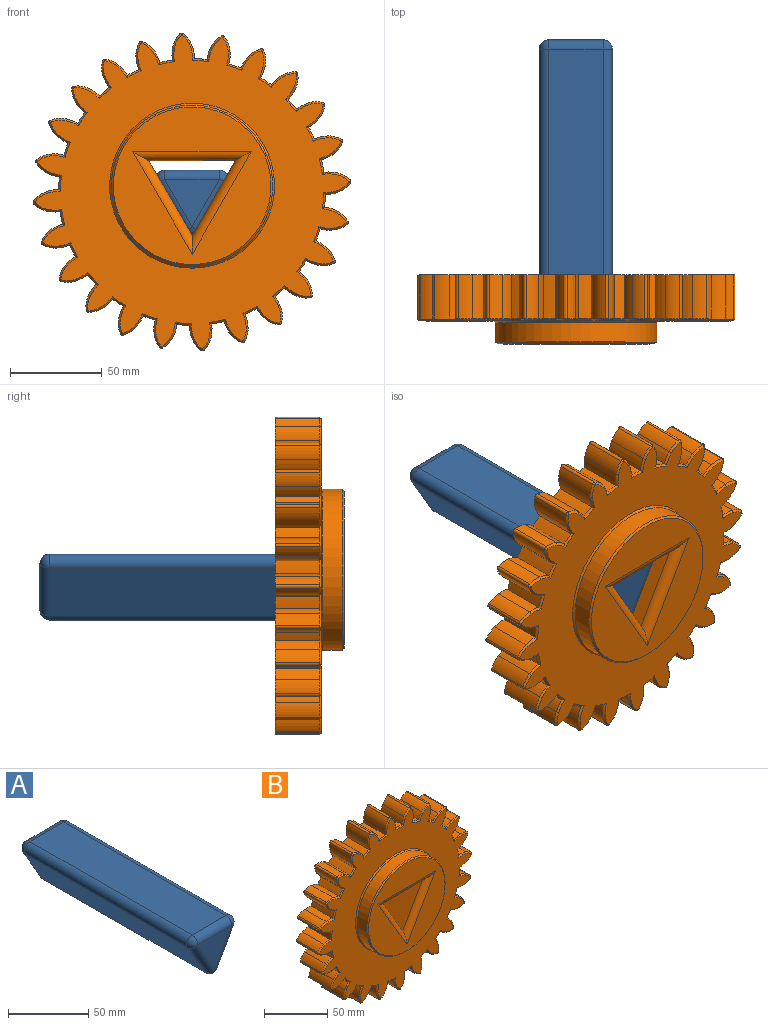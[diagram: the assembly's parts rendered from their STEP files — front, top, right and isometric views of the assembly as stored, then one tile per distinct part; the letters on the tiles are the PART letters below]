
ASSEMBLY  parts=2 mates=1
PART A: 20 faces, bbox 39.9x152.8x35.9 mm
  f0: plane 142.8x29.85mm, normal (0,0,1), area 4262.8mm2, adj f8,f13,f16,f19
  f1: plane 142.8x25.79mm, normal (-0.86,0,-0.5), area 4262.8mm2, adj f6,f14,f15,f19
  f2: plane 142.8x25.91mm, normal (0.87,0,-0.5), area 4262.8mm2, adj f5,f6,f7,f8
  f3: plane 29.85x25.91mm, normal (0,-1,0), area 385.9mm2, adj f5,f13,f14
  f4: plane 29.85x25.91mm, normal (0,1,0), area 385.9mm2, adj f7,f15,f16
  f5: cylinder r=5mm len=28.39mm, axis (-0.5,0,-0.87), area 234.5mm2, adj f2,f3,f9,f10
  f6: cylinder r=5mm len=142.8mm, axis (0,1,0), area 1495.4mm2, adj f1,f2,f10,f11
  f7: cylinder r=5mm len=28.39mm, axis (0.5,0,0.87), area 234.5mm2, adj f2,f4,f11,f12
  f8: cylinder r=5mm len=142.8mm, axis (0,1,0), area 1495.4mm2, adj f0,f2,f9,f12
  f9: sphere r=5mm, area 52.4mm2, adj f5,f8,f13
  f10: sphere r=5mm, area 52.4mm2, adj f5,f6,f14
  f11: sphere r=5mm, area 52.4mm2, adj f6,f7,f15
  f12: sphere r=5mm, area 52.4mm2, adj f7,f8,f16
  f13: cylinder r=5mm len=29.87mm, axis (1,0,0), area 234.5mm2, adj f0,f3,f9,f17
  f14: cylinder r=5mm len=28.31mm, axis (-0.5,0,0.86), area 234.5mm2, adj f1,f3,f10,f17
  f15: cylinder r=5mm len=28.31mm, axis (0.5,0,-0.86), area 234.5mm2, adj f1,f4,f11,f18
  f16: cylinder r=5mm len=29.87mm, axis (-1,0,0), area 234.5mm2, adj f0,f4,f12,f18
  f17: sphere r=5mm, area 52.3mm2, adj f13,f14,f19
  f18: sphere r=5mm, area 52.3mm2, adj f15,f16,f19
  f19: cylinder r=5mm len=142.8mm, axis (0,1,0), area 1495.4mm2, adj f0,f1,f17,f18
PART B: 300 faces, bbox 172.9x37.5x172.9 mm
  f0: cylinder r=72.52mm len=24mm, axis (0,1,0), area 165.9mm2, adj f29,f31,f95,f285
  f1: cylinder r=72.52mm len=24mm, axis (0,1,0), area 165.9mm2, adj f31,f90,f94,f297
  f2: cylinder r=72.52mm len=24mm, axis (0,1,0), area 165.9mm2, adj f31,f85,f89,f286
  f3: cylinder r=72.52mm len=24mm, axis (0,1,0), area 165.9mm2, adj f31,f80,f84,f274
  f4: cylinder r=72.52mm len=24mm, axis (0,1,0), area 165.9mm2, adj f31,f75,f79,f262
  f5: cylinder r=72.52mm len=24mm, axis (0,1,0), area 165.9mm2, adj f31,f70,f74,f250
  f6: cylinder r=72.52mm len=24mm, axis (0,1,0), area 165.9mm2, adj f31,f65,f69,f238
  f7: cylinder r=72.52mm len=24mm, axis (0,1,0), area 165.9mm2, adj f31,f60,f64,f226
  f8: cylinder r=72.52mm len=24mm, axis (0,1,0), area 165.9mm2, adj f31,f55,f59,f214
  f9: cylinder r=72.52mm len=24mm, axis (0,1,0), area 165.9mm2, adj f31,f50,f54,f202
  f10: cylinder r=72.52mm len=24mm, axis (0,1,0), area 165.9mm2, adj f31,f45,f49,f190
  f11: cylinder r=72.52mm len=24mm, axis (0,1,0), area 165.9mm2, adj f31,f40,f44,f178
  f12: cylinder r=72.52mm len=24mm, axis (0,1,0), area 165.9mm2, adj f31,f39,f146,f166
  f13: cylinder r=72.52mm len=24mm, axis (0,1,0), area 165.9mm2, adj f31,f145,f150,f154
  f14: cylinder r=72.52mm len=24mm, axis (0,1,0), area 165.9mm2, adj f31,f140,f144,f165
  f15: cylinder r=72.52mm len=24mm, axis (0,1,0), area 165.9mm2, adj f31,f135,f139,f177
  f16: cylinder r=72.52mm len=24mm, axis (0,1,0), area 165.9mm2, adj f31,f130,f134,f189
  f17: cylinder r=72.52mm len=24mm, axis (0,1,0), area 165.9mm2, adj f31,f125,f129,f201
  f18: cylinder r=72.52mm len=24mm, axis (0,1,0), area 165.9mm2, adj f31,f120,f124,f213
  f19: cylinder r=72.52mm len=24mm, axis (0,1,0), area 165.9mm2, adj f31,f115,f119,f225
  f20: cylinder r=72.52mm len=24mm, axis (0,1,0), area 165.9mm2, adj f31,f110,f114,f237
  f21: cylinder r=72.52mm len=24mm, axis (0,1,0), area 165.9mm2, adj f31,f105,f109,f249
  f22: cylinder r=72.52mm len=24mm, axis (0,1,0), area 165.9mm2, adj f31,f99,f104,f261
  f23: plane 40.76x32.5mm, normal (0.86,0,0.5), area 1533.1mm2, adj f31,f32,f35,f151
  f24: cylinder r=72.52mm len=24mm, axis (0,1,0), area 165.9mm2, adj f25,f31,f100,f273
  f25: cylinder r=18.6mm len=24mm, axis (0,1,0), area 174.8mm2, adj f24,f26,f31,f275
  f26: cylinder r=14.6mm len=24mm, axis (0,1,0), area 191.6mm2, adj f25,f27,f31,f277
  f27: cylinder r=1.39mm len=24mm, axis (0,1,0), area 56.5mm2, adj f26,f28,f31,f279
  f28: cylinder r=14.6mm len=24mm, axis (0,1,0), area 191.6mm2, adj f27,f29,f31,f281
  f29: cylinder r=21.66mm len=24mm, axis (0,1,0), area 174.3mm2, adj f0,f28,f31,f283
  f30: plane 170.88x170.88mm, normal (0,-1,0), area 12366.3mm2, adj f154,f155,f156,f157,f158,f159,f160,f161
  f31: plane 172.88x172.88mm, normal (0,1,0), area 18684mm2, adj f0,f1,f2,f3,f4,f5,f6,f7
  f32: plane 40.94x32.5mm, normal (-0.87,0,0.5), area 1533.1mm2, adj f23,f31,f35,f152
  f33: cylinder r=43.85mm len=87.7mm, axis (0,1,0), area 2892.9mm2, adj f298,f299
  f34: plane 85.7x85.7mm, normal (0,-1,0), area 3967.2mm2, adj f151,f152,f153,f299
  f35: plane 47.17x32.5mm, normal (0,0,-1), area 1533.1mm2, adj f23,f31,f32,f153
  f36: cylinder r=14.6mm len=24mm, axis (0,1,0), area 191.6mm2, adj f31,f37,f40,f174
  f37: cylinder r=1.39mm len=24mm, axis (0,1,0), area 56.5mm2, adj f31,f36,f38,f172
  f38: cylinder r=14.6mm len=24mm, axis (0,1,0), area 191.6mm2, adj f31,f37,f39,f170
  f39: cylinder r=21.66mm len=24mm, axis (0,1,0), area 174.3mm2, adj f12,f31,f38,f168
  f40: cylinder r=18.6mm len=24mm, axis (0,1,0), area 174.8mm2, adj f11,f31,f36,f176
  f41: cylinder r=14.6mm len=24mm, axis (0,1,0), area 191.6mm2, adj f31,f42,f45,f186
  f42: cylinder r=1.39mm len=24mm, axis (0,1,0), area 56.5mm2, adj f31,f41,f43,f184
  f43: cylinder r=14.6mm len=24mm, axis (0,1,0), area 191.6mm2, adj f31,f42,f44,f182
  f44: cylinder r=21.66mm len=24mm, axis (0,1,0), area 174.3mm2, adj f11,f31,f43,f180
  f45: cylinder r=18.6mm len=24mm, axis (0,1,0), area 174.8mm2, adj f10,f31,f41,f188
  f46: cylinder r=14.6mm len=24mm, axis (0,1,0), area 191.6mm2, adj f31,f47,f50,f198
  f47: cylinder r=1.39mm len=24mm, axis (0,1,0), area 56.5mm2, adj f31,f46,f48,f196
  f48: cylinder r=14.6mm len=24mm, axis (0,1,0), area 191.6mm2, adj f31,f47,f49,f194
  f49: cylinder r=21.66mm len=24mm, axis (0,1,0), area 174.3mm2, adj f10,f31,f48,f192
  f50: cylinder r=18.6mm len=24mm, axis (0,1,0), area 174.8mm2, adj f9,f31,f46,f200
  f51: cylinder r=14.6mm len=24mm, axis (0,1,0), area 191.6mm2, adj f31,f52,f55,f210
  f52: cylinder r=1.39mm len=24mm, axis (0,1,0), area 56.5mm2, adj f31,f51,f53,f208
  f53: cylinder r=14.6mm len=24mm, axis (0,1,0), area 191.6mm2, adj f31,f52,f54,f206
  f54: cylinder r=21.66mm len=24mm, axis (0,1,0), area 174.3mm2, adj f9,f31,f53,f204
  f55: cylinder r=18.6mm len=24mm, axis (0,1,0), area 174.8mm2, adj f8,f31,f51,f212
  f56: cylinder r=14.6mm len=24mm, axis (0,1,0), area 191.6mm2, adj f31,f57,f60,f222
  f57: cylinder r=1.39mm len=24mm, axis (0,1,0), area 56.5mm2, adj f31,f56,f58,f220
  f58: cylinder r=14.6mm len=24mm, axis (0,1,0), area 191.6mm2, adj f31,f57,f59,f218
  f59: cylinder r=21.66mm len=24mm, axis (0,1,0), area 174.3mm2, adj f8,f31,f58,f216
  f60: cylinder r=18.6mm len=24mm, axis (0,1,0), area 174.8mm2, adj f7,f31,f56,f224
  f61: cylinder r=14.6mm len=24mm, axis (0,1,0), area 191.6mm2, adj f31,f62,f65,f234
  f62: cylinder r=1.39mm len=24mm, axis (0,1,0), area 56.5mm2, adj f31,f61,f63,f232
  f63: cylinder r=14.6mm len=24mm, axis (0,1,0), area 191.6mm2, adj f31,f62,f64,f230
  f64: cylinder r=21.66mm len=24mm, axis (0,1,0), area 174.3mm2, adj f7,f31,f63,f228
  f65: cylinder r=18.6mm len=24mm, axis (0,1,0), area 174.8mm2, adj f6,f31,f61,f236
  f66: cylinder r=14.6mm len=24mm, axis (0,1,0), area 191.6mm2, adj f31,f67,f70,f246
  f67: cylinder r=1.39mm len=24mm, axis (0,1,0), area 56.5mm2, adj f31,f66,f68,f244
  f68: cylinder r=14.6mm len=24mm, axis (0,1,0), area 191.6mm2, adj f31,f67,f69,f242
  f69: cylinder r=21.66mm len=24mm, axis (0,1,0), area 174.3mm2, adj f6,f31,f68,f240
  f70: cylinder r=18.6mm len=24mm, axis (0,1,0), area 174.8mm2, adj f5,f31,f66,f248
  f71: cylinder r=14.6mm len=24mm, axis (0,1,0), area 191.6mm2, adj f31,f72,f75,f258
  f72: cylinder r=1.39mm len=24mm, axis (0,1,0), area 56.5mm2, adj f31,f71,f73,f256
  f73: cylinder r=14.6mm len=24mm, axis (0,1,0), area 191.6mm2, adj f31,f72,f74,f254
  f74: cylinder r=21.66mm len=24mm, axis (0,1,0), area 174.3mm2, adj f5,f31,f73,f252
  f75: cylinder r=18.6mm len=24mm, axis (0,1,0), area 174.8mm2, adj f4,f31,f71,f260
  f76: cylinder r=14.6mm len=24mm, axis (0,1,0), area 191.6mm2, adj f31,f77,f80,f270
  f77: cylinder r=1.39mm len=24mm, axis (0,1,0), area 56.5mm2, adj f31,f76,f78,f268
  f78: cylinder r=14.6mm len=24mm, axis (0,1,0), area 191.6mm2, adj f31,f77,f79,f266
  f79: cylinder r=21.66mm len=24mm, axis (0,1,0), area 174.3mm2, adj f4,f31,f78,f264
  f80: cylinder r=18.6mm len=24mm, axis (0,1,0), area 174.8mm2, adj f3,f31,f76,f272
  f81: cylinder r=14.6mm len=24mm, axis (0,1,0), area 191.6mm2, adj f31,f82,f85,f282
  f82: cylinder r=1.39mm len=24mm, axis (0,1,0), area 56.5mm2, adj f31,f81,f83,f280
  f83: cylinder r=14.6mm len=24mm, axis (0,1,0), area 191.6mm2, adj f31,f82,f84,f278
  f84: cylinder r=21.66mm len=24mm, axis (0,1,0), area 174.3mm2, adj f3,f31,f83,f276
  f85: cylinder r=18.6mm len=24mm, axis (0,1,0), area 174.8mm2, adj f2,f31,f81,f284
  f86: cylinder r=14.6mm len=24mm, axis (0,1,0), area 191.6mm2, adj f31,f87,f90,f294
  f87: cylinder r=1.39mm len=24mm, axis (0,1,0), area 56.5mm2, adj f31,f86,f88,f292
  f88: cylinder r=14.6mm len=24mm, axis (0,1,0), area 191.6mm2, adj f31,f87,f89,f290
  f89: cylinder r=21.66mm len=24mm, axis (0,1,0), area 174.3mm2, adj f2,f31,f88,f288
  f90: cylinder r=18.6mm len=24mm, axis (0,1,0), area 174.8mm2, adj f1,f31,f86,f296
  f91: cylinder r=14.6mm len=24mm, axis (0,1,0), area 191.6mm2, adj f31,f92,f95,f289
  f92: cylinder r=1.39mm len=24mm, axis (0,1,0), area 56.5mm2, adj f31,f91,f93,f291
  f93: cylinder r=14.6mm len=24mm, axis (0,1,0), area 191.6mm2, adj f31,f92,f94,f293
  f94: cylinder r=21.66mm len=24mm, axis (0,1,0), area 174.3mm2, adj f1,f31,f93,f295
  f95: cylinder r=18.6mm len=24mm, axis (0,1,0), area 174.8mm2, adj f0,f31,f91,f287
  f96: cylinder r=14.6mm len=24mm, axis (0,1,0), area 191.6mm2, adj f31,f97,f99,f265
  f97: cylinder r=1.39mm len=24mm, axis (0,1,0), area 56.5mm2, adj f31,f96,f98,f267
  f98: cylinder r=14.6mm len=24mm, axis (0,1,0), area 191.6mm2, adj f31,f97,f100,f269
  f99: cylinder r=18.6mm len=24mm, axis (0,1,0), area 174.8mm2, adj f22,f31,f96,f263
  f100: cylinder r=21.66mm len=24mm, axis (0,1,0), area 174.3mm2, adj f24,f31,f98,f271
  f101: cylinder r=14.6mm len=24mm, axis (0,1,0), area 191.6mm2, adj f31,f102,f105,f253
  f102: cylinder r=1.39mm len=24mm, axis (0,1,0), area 56.5mm2, adj f31,f101,f103,f255
  f103: cylinder r=14.6mm len=24mm, axis (0,1,0), area 191.6mm2, adj f31,f102,f104,f257
  f104: cylinder r=21.66mm len=24mm, axis (0,1,0), area 174.3mm2, adj f22,f31,f103,f259
  f105: cylinder r=18.6mm len=24mm, axis (0,1,0), area 174.8mm2, adj f21,f31,f101,f251
  f106: cylinder r=14.6mm len=24mm, axis (0,1,0), area 191.6mm2, adj f31,f107,f110,f241
  f107: cylinder r=1.39mm len=24mm, axis (0,1,0), area 56.5mm2, adj f31,f106,f108,f243
  f108: cylinder r=14.6mm len=24mm, axis (0,1,0), area 191.6mm2, adj f31,f107,f109,f245
  f109: cylinder r=21.66mm len=24mm, axis (0,1,0), area 174.3mm2, adj f21,f31,f108,f247
  f110: cylinder r=18.6mm len=24mm, axis (0,1,0), area 174.8mm2, adj f20,f31,f106,f239
  f111: cylinder r=14.6mm len=24mm, axis (0,1,0), area 191.6mm2, adj f31,f112,f115,f229
  f112: cylinder r=1.39mm len=24mm, axis (0,1,0), area 56.5mm2, adj f31,f111,f113,f231
  f113: cylinder r=14.6mm len=24mm, axis (0,1,0), area 191.6mm2, adj f31,f112,f114,f233
  f114: cylinder r=21.66mm len=24mm, axis (0,1,0), area 174.3mm2, adj f20,f31,f113,f235
  f115: cylinder r=18.6mm len=24mm, axis (0,1,0), area 174.8mm2, adj f19,f31,f111,f227
  f116: cylinder r=14.6mm len=24mm, axis (0,1,0), area 191.6mm2, adj f31,f117,f120,f217
  f117: cylinder r=1.39mm len=24mm, axis (0,1,0), area 56.5mm2, adj f31,f116,f118,f219
  f118: cylinder r=14.6mm len=24mm, axis (0,1,0), area 191.6mm2, adj f31,f117,f119,f221
  f119: cylinder r=21.66mm len=24mm, axis (0,1,0), area 174.3mm2, adj f19,f31,f118,f223
  f120: cylinder r=18.6mm len=24mm, axis (0,1,0), area 174.8mm2, adj f18,f31,f116,f215
  f121: cylinder r=14.6mm len=24mm, axis (0,1,0), area 191.6mm2, adj f31,f122,f125,f205
  f122: cylinder r=1.39mm len=24mm, axis (0,1,0), area 56.5mm2, adj f31,f121,f123,f207
  f123: cylinder r=14.6mm len=24mm, axis (0,1,0), area 191.6mm2, adj f31,f122,f124,f209
  f124: cylinder r=21.66mm len=24mm, axis (0,1,0), area 174.3mm2, adj f18,f31,f123,f211
  f125: cylinder r=18.6mm len=24mm, axis (0,1,0), area 174.8mm2, adj f17,f31,f121,f203
  f126: cylinder r=14.6mm len=24mm, axis (0,1,0), area 191.6mm2, adj f31,f127,f130,f193
  f127: cylinder r=1.39mm len=24mm, axis (0,1,0), area 56.5mm2, adj f31,f126,f128,f195
  f128: cylinder r=14.6mm len=24mm, axis (0,1,0), area 191.6mm2, adj f31,f127,f129,f197
  f129: cylinder r=21.66mm len=24mm, axis (0,1,0), area 174.3mm2, adj f17,f31,f128,f199
  f130: cylinder r=18.6mm len=24mm, axis (0,1,0), area 174.8mm2, adj f16,f31,f126,f191
  f131: cylinder r=14.6mm len=24mm, axis (0,1,0), area 191.6mm2, adj f31,f132,f135,f181
  f132: cylinder r=1.39mm len=24mm, axis (0,1,0), area 56.5mm2, adj f31,f131,f133,f183
  f133: cylinder r=14.6mm len=24mm, axis (0,1,0), area 191.6mm2, adj f31,f132,f134,f185
  f134: cylinder r=21.66mm len=24mm, axis (0,1,0), area 174.3mm2, adj f16,f31,f133,f187
  f135: cylinder r=18.6mm len=24mm, axis (0,1,0), area 174.8mm2, adj f15,f31,f131,f179
  f136: cylinder r=14.6mm len=24mm, axis (0,1,0), area 191.6mm2, adj f31,f137,f140,f169
  f137: cylinder r=1.39mm len=24mm, axis (0,1,0), area 56.5mm2, adj f31,f136,f138,f171
  f138: cylinder r=14.6mm len=24mm, axis (0,1,0), area 191.6mm2, adj f31,f137,f139,f173
  f139: cylinder r=21.66mm len=24mm, axis (0,1,0), area 174.3mm2, adj f15,f31,f138,f175
  f140: cylinder r=18.6mm len=24mm, axis (0,1,0), area 174.8mm2, adj f14,f31,f136,f167
  f141: cylinder r=14.6mm len=24mm, axis (0,1,0), area 191.6mm2, adj f31,f142,f145,f157
  f142: cylinder r=1.39mm len=24mm, axis (0,1,0), area 56.5mm2, adj f31,f141,f143,f159
  f143: cylinder r=14.6mm len=24mm, axis (0,1,0), area 191.6mm2, adj f31,f142,f144,f161
  f144: cylinder r=21.66mm len=24mm, axis (0,1,0), area 174.3mm2, adj f14,f31,f143,f163
  f145: cylinder r=18.6mm len=24mm, axis (0,1,0), area 174.8mm2, adj f13,f31,f141,f155
  f146: cylinder r=18.6mm len=24mm, axis (0,1,0), area 174.8mm2, adj f12,f31,f147,f164
  f147: cylinder r=14.6mm len=24mm, axis (0,1,0), area 191.6mm2, adj f31,f146,f148,f162
  f148: cylinder r=1.39mm len=24mm, axis (0,1,0), area 56.5mm2, adj f31,f147,f149,f160
  f149: cylinder r=14.6mm len=24mm, axis (0,1,0), area 191.6mm2, adj f31,f148,f150,f158
  f150: cylinder r=21.66mm len=24mm, axis (0,1,0), area 174.3mm2, adj f13,f31,f149,f156
  f151: cylinder r=5mm len=58.24mm, axis (0.5,0,-0.86), area 419.9mm2, adj f23,f34,f152,f153
  f152: cylinder r=5mm len=58.46mm, axis (0.5,0,0.87), area 419.9mm2, adj f32,f34,f151,f153
  f153: cylinder r=5mm len=64.51mm, axis (-1,0,0), area 419.9mm2, adj f34,f35,f151,f152
  f154: cone r=71.52mm half-angle=45deg, axis (0,1,0), area 11.1mm2, adj f13,f30,f155,f156
  f155: cone r=17.6mm half-angle=45deg, axis (0,1,0), area 10.8mm2, adj f30,f145,f154,f157
  f156: cone r=20.66mm half-angle=45deg, axis (0,1,0), area 10.7mm2, adj f30,f150,f154,f158
  f157: cone r=13.6mm half-angle=45deg, axis (0,1,0), area 11mm2, adj f30,f141,f155,f159
  f158: cone r=14.6mm half-angle=45deg, axis (0,1,0), area 11mm2, adj f30,f149,f156,f160
  f159: cone r=0.39mm half-angle=45deg, axis (0,1,0), area 2.2mm2, adj f30,f142,f157,f161
  f160: cone r=0.39mm half-angle=45deg, axis (0,1,0), area 2.2mm2, adj f30,f148,f158,f162
  f161: cone r=14.6mm half-angle=45deg, axis (0,1,0), area 11mm2, adj f30,f143,f159,f163
  f162: cone r=13.6mm half-angle=45deg, axis (0,1,0), area 11mm2, adj f30,f147,f160,f164
  f163: cone r=20.66mm half-angle=45deg, axis (0,1,0), area 10.7mm2, adj f30,f144,f161,f165
  f164: cone r=17.6mm half-angle=45deg, axis (0,1,0), area 10.8mm2, adj f30,f146,f162,f166
  f165: cone r=71.52mm half-angle=45deg, axis (0,1,0), area 11.1mm2, adj f14,f30,f163,f167
  f166: cone r=71.52mm half-angle=45deg, axis (0,1,0), area 11.1mm2, adj f12,f30,f164,f168
  f167: cone r=17.6mm half-angle=45deg, axis (0,1,0), area 10.8mm2, adj f30,f140,f165,f169
  f168: cone r=20.66mm half-angle=45deg, axis (0,1,0), area 10.7mm2, adj f30,f39,f166,f170
  f169: cone r=13.6mm half-angle=45deg, axis (0,1,0), area 11mm2, adj f30,f136,f167,f171
  f170: cone r=14.6mm half-angle=45deg, axis (0,1,0), area 11mm2, adj f30,f38,f168,f172
  f171: cone r=0.39mm half-angle=45deg, axis (0,1,0), area 2.2mm2, adj f30,f137,f169,f173
  f172: cone r=0.39mm half-angle=45deg, axis (0,1,0), area 2.2mm2, adj f30,f37,f170,f174
  f173: cone r=14.6mm half-angle=45deg, axis (0,1,0), area 11mm2, adj f30,f138,f171,f175
  f174: cone r=13.6mm half-angle=45deg, axis (0,1,0), area 11mm2, adj f30,f36,f172,f176
  f175: cone r=20.66mm half-angle=45deg, axis (0,1,0), area 10.7mm2, adj f30,f139,f173,f177
  f176: cone r=17.6mm half-angle=45deg, axis (0,1,0), area 10.8mm2, adj f30,f40,f174,f178
  f177: cone r=71.52mm half-angle=45deg, axis (0,1,0), area 11.1mm2, adj f15,f30,f175,f179
  f178: cone r=71.52mm half-angle=45deg, axis (0,1,0), area 11.1mm2, adj f11,f30,f176,f180
  f179: cone r=17.6mm half-angle=45deg, axis (0,1,0), area 10.8mm2, adj f30,f135,f177,f181
  f180: cone r=20.66mm half-angle=45deg, axis (0,1,0), area 10.7mm2, adj f30,f44,f178,f182
  f181: cone r=13.6mm half-angle=45deg, axis (0,1,0), area 11mm2, adj f30,f131,f179,f183
  f182: cone r=14.6mm half-angle=45deg, axis (0,1,0), area 11mm2, adj f30,f43,f180,f184
  f183: cone r=0.39mm half-angle=45deg, axis (0,1,0), area 2.2mm2, adj f30,f132,f181,f185
  f184: cone r=0.39mm half-angle=45deg, axis (0,1,0), area 2.2mm2, adj f30,f42,f182,f186
  f185: cone r=14.6mm half-angle=45deg, axis (0,1,0), area 11mm2, adj f30,f133,f183,f187
  f186: cone r=13.6mm half-angle=45deg, axis (0,1,0), area 11mm2, adj f30,f41,f184,f188
  f187: cone r=20.66mm half-angle=45deg, axis (0,1,0), area 10.7mm2, adj f30,f134,f185,f189
  f188: cone r=17.6mm half-angle=45deg, axis (0,1,0), area 10.8mm2, adj f30,f45,f186,f190
  f189: cone r=71.52mm half-angle=45deg, axis (0,1,0), area 11.1mm2, adj f16,f30,f187,f191
  f190: cone r=71.52mm half-angle=45deg, axis (0,1,0), area 11.1mm2, adj f10,f30,f188,f192
  f191: cone r=17.6mm half-angle=45deg, axis (0,1,0), area 10.8mm2, adj f30,f130,f189,f193
  f192: cone r=20.66mm half-angle=45deg, axis (0,1,0), area 10.7mm2, adj f30,f49,f190,f194
  f193: cone r=13.6mm half-angle=45deg, axis (0,1,0), area 11mm2, adj f30,f126,f191,f195
  f194: cone r=14.6mm half-angle=45deg, axis (0,1,0), area 11mm2, adj f30,f48,f192,f196
  f195: cone r=0.39mm half-angle=45deg, axis (0,1,0), area 2.2mm2, adj f30,f127,f193,f197
  f196: cone r=0.39mm half-angle=45deg, axis (0,1,0), area 2.2mm2, adj f30,f47,f194,f198
  f197: cone r=14.6mm half-angle=45deg, axis (0,1,0), area 11mm2, adj f30,f128,f195,f199
  f198: cone r=13.6mm half-angle=45deg, axis (0,1,0), area 11mm2, adj f30,f46,f196,f200
  f199: cone r=20.66mm half-angle=45deg, axis (0,1,0), area 10.7mm2, adj f30,f129,f197,f201
  f200: cone r=17.6mm half-angle=45deg, axis (0,1,0), area 10.8mm2, adj f30,f50,f198,f202
  f201: cone r=71.52mm half-angle=45deg, axis (0,1,0), area 11.1mm2, adj f17,f30,f199,f203
  f202: cone r=71.52mm half-angle=45deg, axis (0,1,0), area 11.1mm2, adj f9,f30,f200,f204
  f203: cone r=17.6mm half-angle=45deg, axis (0,1,0), area 10.8mm2, adj f30,f125,f201,f205
  f204: cone r=20.66mm half-angle=45deg, axis (0,1,0), area 10.7mm2, adj f30,f54,f202,f206
  f205: cone r=13.6mm half-angle=45deg, axis (0,1,0), area 11mm2, adj f30,f121,f203,f207
  f206: cone r=14.6mm half-angle=45deg, axis (0,1,0), area 11mm2, adj f30,f53,f204,f208
  f207: cone r=0.39mm half-angle=45deg, axis (0,1,0), area 2.2mm2, adj f30,f122,f205,f209
  f208: cone r=0.39mm half-angle=45deg, axis (0,1,0), area 2.2mm2, adj f30,f52,f206,f210
  f209: cone r=14.6mm half-angle=45deg, axis (0,1,0), area 11mm2, adj f30,f123,f207,f211
  f210: cone r=13.6mm half-angle=45deg, axis (0,1,0), area 11mm2, adj f30,f51,f208,f212
  f211: cone r=20.66mm half-angle=45deg, axis (0,1,0), area 10.7mm2, adj f30,f124,f209,f213
  f212: cone r=17.6mm half-angle=45deg, axis (0,1,0), area 10.8mm2, adj f30,f55,f210,f214
  f213: cone r=71.52mm half-angle=45deg, axis (0,1,0), area 11.1mm2, adj f18,f30,f211,f215
  f214: cone r=71.52mm half-angle=45deg, axis (0,1,0), area 11.1mm2, adj f8,f30,f212,f216
  f215: cone r=17.6mm half-angle=45deg, axis (0,1,0), area 10.8mm2, adj f30,f120,f213,f217
  f216: cone r=20.66mm half-angle=45deg, axis (0,1,0), area 10.7mm2, adj f30,f59,f214,f218
  f217: cone r=13.6mm half-angle=45deg, axis (0,1,0), area 11mm2, adj f30,f116,f215,f219
  f218: cone r=14.6mm half-angle=45deg, axis (0,1,0), area 11mm2, adj f30,f58,f216,f220
  f219: cone r=0.39mm half-angle=45deg, axis (0,1,0), area 2.2mm2, adj f30,f117,f217,f221
  f220: cone r=0.39mm half-angle=45deg, axis (0,1,0), area 2.2mm2, adj f30,f57,f218,f222
  f221: cone r=14.6mm half-angle=45deg, axis (0,1,0), area 11mm2, adj f30,f118,f219,f223
  f222: cone r=13.6mm half-angle=45deg, axis (0,1,0), area 11mm2, adj f30,f56,f220,f224
  f223: cone r=20.66mm half-angle=45deg, axis (0,1,0), area 10.7mm2, adj f30,f119,f221,f225
  f224: cone r=17.6mm half-angle=45deg, axis (0,1,0), area 10.8mm2, adj f30,f60,f222,f226
  f225: cone r=71.52mm half-angle=45deg, axis (0,1,0), area 11.1mm2, adj f19,f30,f223,f227
  f226: cone r=71.52mm half-angle=45deg, axis (0,1,0), area 11.1mm2, adj f7,f30,f224,f228
  f227: cone r=17.6mm half-angle=45deg, axis (0,1,0), area 10.8mm2, adj f30,f115,f225,f229
  f228: cone r=20.66mm half-angle=45deg, axis (0,1,0), area 10.7mm2, adj f30,f64,f226,f230
  f229: cone r=13.6mm half-angle=45deg, axis (0,1,0), area 11mm2, adj f30,f111,f227,f231
  f230: cone r=14.6mm half-angle=45deg, axis (0,1,0), area 11mm2, adj f30,f63,f228,f232
  f231: cone r=0.39mm half-angle=45deg, axis (0,1,0), area 2.2mm2, adj f30,f112,f229,f233
  f232: cone r=0.39mm half-angle=45deg, axis (0,1,0), area 2.2mm2, adj f30,f62,f230,f234
  f233: cone r=14.6mm half-angle=45deg, axis (0,1,0), area 11mm2, adj f30,f113,f231,f235
  f234: cone r=13.6mm half-angle=45deg, axis (0,1,0), area 11mm2, adj f30,f61,f232,f236
  f235: cone r=20.66mm half-angle=45deg, axis (0,1,0), area 10.7mm2, adj f30,f114,f233,f237
  f236: cone r=17.6mm half-angle=45deg, axis (0,1,0), area 10.8mm2, adj f30,f65,f234,f238
  f237: cone r=71.52mm half-angle=45deg, axis (0,1,0), area 11.1mm2, adj f20,f30,f235,f239
  f238: cone r=71.52mm half-angle=45deg, axis (0,1,0), area 11.1mm2, adj f6,f30,f236,f240
  f239: cone r=17.6mm half-angle=45deg, axis (0,1,0), area 10.8mm2, adj f30,f110,f237,f241
  f240: cone r=20.66mm half-angle=45deg, axis (0,1,0), area 10.7mm2, adj f30,f69,f238,f242
  f241: cone r=13.6mm half-angle=45deg, axis (0,1,0), area 11mm2, adj f30,f106,f239,f243
  f242: cone r=14.6mm half-angle=45deg, axis (0,1,0), area 11mm2, adj f30,f68,f240,f244
  f243: cone r=0.39mm half-angle=45deg, axis (0,1,0), area 2.2mm2, adj f30,f107,f241,f245
  f244: cone r=0.39mm half-angle=45deg, axis (0,1,0), area 2.2mm2, adj f30,f67,f242,f246
  f245: cone r=14.6mm half-angle=45deg, axis (0,1,0), area 11mm2, adj f30,f108,f243,f247
  f246: cone r=13.6mm half-angle=45deg, axis (0,1,0), area 11mm2, adj f30,f66,f244,f248
  f247: cone r=20.66mm half-angle=45deg, axis (0,1,0), area 10.7mm2, adj f30,f109,f245,f249
  f248: cone r=17.6mm half-angle=45deg, axis (0,1,0), area 10.8mm2, adj f30,f70,f246,f250
  f249: cone r=71.52mm half-angle=45deg, axis (0,1,0), area 11.1mm2, adj f21,f30,f247,f251
  f250: cone r=71.52mm half-angle=45deg, axis (0,1,0), area 11.1mm2, adj f5,f30,f248,f252
  f251: cone r=17.6mm half-angle=45deg, axis (0,1,0), area 10.8mm2, adj f30,f105,f249,f253
  f252: cone r=20.66mm half-angle=45deg, axis (0,1,0), area 10.7mm2, adj f30,f74,f250,f254
  f253: cone r=13.6mm half-angle=45deg, axis (0,1,0), area 11mm2, adj f30,f101,f251,f255
  f254: cone r=14.6mm half-angle=45deg, axis (0,1,0), area 11mm2, adj f30,f73,f252,f256
  f255: cone r=0.39mm half-angle=45deg, axis (0,1,0), area 2.2mm2, adj f30,f102,f253,f257
  f256: cone r=0.39mm half-angle=45deg, axis (0,1,0), area 2.2mm2, adj f30,f72,f254,f258
  f257: cone r=14.6mm half-angle=45deg, axis (0,1,0), area 11mm2, adj f30,f103,f255,f259
  f258: cone r=13.6mm half-angle=45deg, axis (0,1,0), area 11mm2, adj f30,f71,f256,f260
  f259: cone r=20.66mm half-angle=45deg, axis (0,1,0), area 10.7mm2, adj f30,f104,f257,f261
  f260: cone r=17.6mm half-angle=45deg, axis (0,1,0), area 10.8mm2, adj f30,f75,f258,f262
  f261: cone r=71.52mm half-angle=45deg, axis (0,1,0), area 11.1mm2, adj f22,f30,f259,f263
  f262: cone r=71.52mm half-angle=45deg, axis (0,1,0), area 11.1mm2, adj f4,f30,f260,f264
  f263: cone r=17.6mm half-angle=45deg, axis (0,1,0), area 10.8mm2, adj f30,f99,f261,f265
  f264: cone r=20.66mm half-angle=45deg, axis (0,1,0), area 10.7mm2, adj f30,f79,f262,f266
  f265: cone r=13.6mm half-angle=45deg, axis (0,1,0), area 11mm2, adj f30,f96,f263,f267
  f266: cone r=14.6mm half-angle=45deg, axis (0,1,0), area 11mm2, adj f30,f78,f264,f268
  f267: cone r=0.39mm half-angle=45deg, axis (0,1,0), area 2.2mm2, adj f30,f97,f265,f269
  f268: cone r=0.39mm half-angle=45deg, axis (0,1,0), area 2.2mm2, adj f30,f77,f266,f270
  f269: cone r=14.6mm half-angle=45deg, axis (0,1,0), area 11mm2, adj f30,f98,f267,f271
  f270: cone r=13.6mm half-angle=45deg, axis (0,1,0), area 11mm2, adj f30,f76,f268,f272
  f271: cone r=20.66mm half-angle=45deg, axis (0,1,0), area 10.7mm2, adj f30,f100,f269,f273
  f272: cone r=17.6mm half-angle=45deg, axis (0,1,0), area 10.8mm2, adj f30,f80,f270,f274
  f273: cone r=71.52mm half-angle=45deg, axis (0,1,0), area 11.1mm2, adj f24,f30,f271,f275
  f274: cone r=71.52mm half-angle=45deg, axis (0,1,0), area 11.1mm2, adj f3,f30,f272,f276
  f275: cone r=17.6mm half-angle=45deg, axis (0,1,0), area 10.8mm2, adj f25,f30,f273,f277
  f276: cone r=20.66mm half-angle=45deg, axis (0,1,0), area 10.7mm2, adj f30,f84,f274,f278
  f277: cone r=13.6mm half-angle=45deg, axis (0,1,0), area 11mm2, adj f26,f30,f275,f279
  f278: cone r=14.6mm half-angle=45deg, axis (0,1,0), area 11mm2, adj f30,f83,f276,f280
  f279: cone r=0.39mm half-angle=45deg, axis (0,1,0), area 2.2mm2, adj f27,f30,f277,f281
  f280: cone r=0.39mm half-angle=45deg, axis (0,1,0), area 2.2mm2, adj f30,f82,f278,f282
  f281: cone r=14.6mm half-angle=45deg, axis (0,1,0), area 11mm2, adj f28,f30,f279,f283
  f282: cone r=13.6mm half-angle=45deg, axis (0,1,0), area 11mm2, adj f30,f81,f280,f284
  f283: cone r=20.66mm half-angle=45deg, axis (0,1,0), area 10.7mm2, adj f29,f30,f281,f285
  f284: cone r=17.6mm half-angle=45deg, axis (0,1,0), area 10.8mm2, adj f30,f85,f282,f286
  f285: cone r=71.52mm half-angle=45deg, axis (0,1,0), area 11.1mm2, adj f0,f30,f283,f287
  f286: cone r=71.52mm half-angle=45deg, axis (0,1,0), area 11.1mm2, adj f2,f30,f284,f288
  f287: cone r=17.6mm half-angle=45deg, axis (0,1,0), area 10.8mm2, adj f30,f95,f285,f289
  f288: cone r=20.66mm half-angle=45deg, axis (0,1,0), area 10.7mm2, adj f30,f89,f286,f290
  f289: cone r=13.6mm half-angle=45deg, axis (0,1,0), area 11mm2, adj f30,f91,f287,f291
  f290: cone r=14.6mm half-angle=45deg, axis (0,1,0), area 11mm2, adj f30,f88,f288,f292
  f291: cone r=0.39mm half-angle=45deg, axis (0,1,0), area 2.2mm2, adj f30,f92,f289,f293
  f292: cone r=0.39mm half-angle=45deg, axis (0,1,0), area 2.2mm2, adj f30,f87,f290,f294
  f293: cone r=14.6mm half-angle=45deg, axis (0,1,0), area 11mm2, adj f30,f93,f291,f295
  f294: cone r=13.6mm half-angle=45deg, axis (0,1,0), area 11mm2, adj f30,f86,f292,f296
  f295: cone r=20.66mm half-angle=45deg, axis (0,1,0), area 10.7mm2, adj f30,f94,f293,f297
  f296: cone r=17.6mm half-angle=45deg, axis (0,1,0), area 10.8mm2, adj f30,f90,f294,f297
  f297: cone r=71.52mm half-angle=45deg, axis (0,1,0), area 11.1mm2, adj f1,f30,f295,f296
  f298: cone r=44.85mm half-angle=45deg, axis (0,1,0), area 394.1mm2, adj f30,f33
  f299: cone r=42.85mm half-angle=45deg, axis (0,1,0), area 385.2mm2, adj f33,f34
PLACE A rot(axis=(-0.39,-0.54,0.75),0deg) t=(5.99,158.43,2.38)mm
PLACE B rot(axis=(-0.39,-0.54,0.75),0deg) t=(6.5,94.53,6.57)mm
MATE slider A.f3 <-> B.f30  axis (0,-1,0) through (6.43,82.03,1.37)mm
